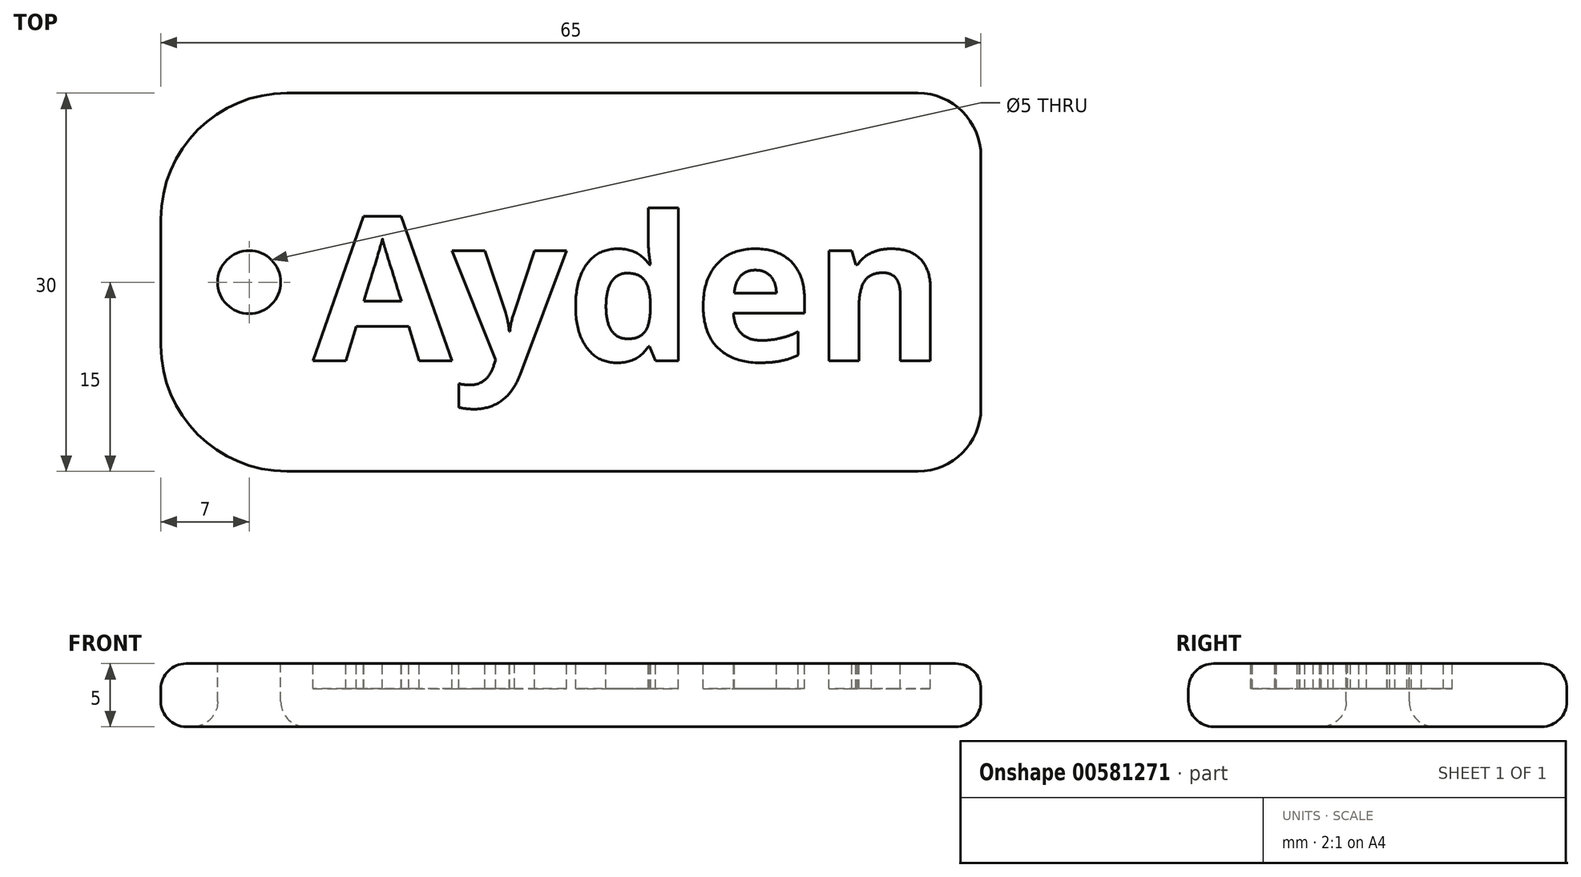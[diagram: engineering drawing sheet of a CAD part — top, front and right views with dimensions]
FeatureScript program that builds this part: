
annotation { "Feature Type Name" : "Feature", "Feature Type Description" : "" }
export const myFeature = defineFeature(function(context is Context, id is Id, definition is map)
    precondition{}
    {
        {
            var Q0;
            Q0=qCreatedBy(makeId("Top.planeOp"),FACE);
            var sketch = newSketch(context, id + "F0", { "sketchPlane" : qUnion([Q0])});
            skLineSegment(sketch, "E0.bottom", {"start": v(0, 0) * mm, "end": v(65, 0) * mm});
            skLineSegment(sketch, "E0.top", {"start": v(0, 30) * mm, "end": v(65, 30) * mm});
            skLineSegment(sketch, "E0.left", {"start": v(0, 0) * mm, "end": v(0, 30) * mm});
            skLineSegment(sketch, "E0.right", {"start": v(65, 0) * mm, "end": v(65, 30) * mm});
            skSolve(sketch);
        }
        {
            var Q0;
            Q0=makeQuery(id+"F0.imprint","IMPRINT",FACE,{"disambiguationData":[TD([[makeQuery(id+"F0.imprint","IMPRINT",EDGE,{"derivedFrom":sQuery(id+"F0.wireOp",EDGE,"E0.bottom")}),1.0]])]});
            extrude(context, id + "F1", {"entities" : qUnion([Q0]), "depth" : 5 * mm, "offsetDistance" : 25 * mm});
        }
        {
            var Q0;
            Q0=makeQuery(id+"F1.opExtrude","CAP_FACE",FACE,{"disambiguationData":[OSD([sQuery(id+"F0.wireOp",EDGE,"E0.bottom"),sQuery(id+"F0.wireOp",EDGE,"E0.top"),sQuery(id+"F0.wireOp",EDGE,"E0.left"),sQuery(id+"F0.wireOp",EDGE,"E0.right")])],"isStart":false});
            var sketch = newSketch(context, id + "F2", { "sketchPlane" : qUnion([Q0])});
            skCircle(sketch, "E1", {"center": v(7, 15) * mm, "radius": 2.5 * mm});
            skPoint(sketch, "E1.centerSnap0", {"position": v(0, 15) * mm});
            skSolve(sketch);
        }
        {
            var Q0;
            Q0=makeQuery(id+"F2.imprint","IMPRINT",FACE,{"disambiguationData":[TD([[makeQuery(id+"F2.imprint","IMPRINT",EDGE,{"derivedFrom":sQuery(id+"F2.wireOp",EDGE,"E1")}),1.0]])]});
            extrude(context, id + "F3", {"entities" : qUnion([Q0]), "operationType" : NewBodyOperationType.REMOVE, "endBound" : BoundingType.THROUGH_ALL, "oppositeDirection" : true, "depth" : 25 * mm, "offsetDistance" : 25 * mm});
        }
        {
            var Q0;
            Q0=makeQuery(id+"F1.opExtrude","SWEPT_EDGE",EDGE,{"disambiguationData":[OSD([sQuery(id+"F0.wireOp",EDGE,"E0.top"),sQuery(id+"F0.wireOp",EDGE,"E0.right")])]});
            var Q1;
            Q1=makeQuery(id+"F1.opExtrude","SWEPT_EDGE",EDGE,{"disambiguationData":[OSD([sQuery(id+"F0.wireOp",EDGE,"E0.bottom"),sQuery(id+"F0.wireOp",EDGE,"E0.right")])]});
            fillet(context, id + "F4", {"entities" : qUnion([Q0, Q1]), "radius" : 5 * mm, "tangentPropagation" : true, "allowEdgeOverflow" : false});
        }
        {
            var Q0;
            Q0=makeQuery(id+"F1.opExtrude","SWEPT_EDGE",EDGE,{"disambiguationData":[OSD([sQuery(id+"F0.wireOp",EDGE,"E0.top"),sQuery(id+"F0.wireOp",EDGE,"E0.left")])]});
            var Q1;
            Q1=makeQuery(id+"F1.opExtrude","SWEPT_EDGE",EDGE,{"disambiguationData":[OSD([sQuery(id+"F0.wireOp",EDGE,"E0.bottom"),sQuery(id+"F0.wireOp",EDGE,"E0.left")])]});
            fillet(context, id + "F5", {"entities" : qUnion([Q0, Q1]), "radius" : 10 * mm, "tangentPropagation" : true, "allowEdgeOverflow" : false});
        }
        {
            var Q0;
            Q0=makeQuery(id+"F1.opExtrude","CAP_FACE",FACE,{"disambiguationData":[OSD([sQuery(id+"F0.wireOp",EDGE,"E0.bottom"),sQuery(id+"F0.wireOp",EDGE,"E0.top"),sQuery(id+"F0.wireOp",EDGE,"E0.left"),sQuery(id+"F0.wireOp",EDGE,"E0.right")])],"isStart":false});
            var sketch = newSketch(context, id + "F6", { "sketchPlane" : qUnion([Q0])});
            skText(sketch, "E2", { "text": "Ayden", "fontName": "OpenSans-Bold.ttf"});
            const initialGuessF6  = {"E2": [0.01205, 0.00877, 1, 0, 0.0115]};
            skSetInitialGuess(sketch, initialGuessF6);
            skSolve(sketch);
        }
        {
            var Q0;
            Q0 = qSketchRegion(id + "F6", true);
            extrude(context, id + "F7", {"entities" : qUnion([Q0]), "operationType" : NewBodyOperationType.REMOVE, "oppositeDirection" : true, "depth" : 2 * mm, "offsetDistance" : 25 * mm});
        }
        {
            var Q0;
            Q0=makeQuery(id+"F1.opExtrude","CAP_EDGE",EDGE,{"disambiguationData":[OSD([sQuery(id+"F0.wireOp",EDGE,"E0.top")])],"isStart":false});
            var Q1;
            {var subQ0=sQuery(id+"F0.wireOp",EDGE,"E0.right");var subQ1=sQuery(id+"F0.wireOp",EDGE,"E0.top");Q1=makeQuery(id+"F4.opFillet","BLEND_EDGE",EDGE,{"blendedFrom":[makeQuery(id+"F1.opExtrude","SWEPT_EDGE",EDGE,{"disambiguationData":[OSD([subQ1,subQ0])]}),makeQuery(id+"F1.opExtrude","CAP_FACE",FACE,{"disambiguationData":[OSD([sQuery(id+"F0.wireOp",EDGE,"E0.bottom"),subQ1,sQuery(id+"F0.wireOp",EDGE,"E0.left"),subQ0])],"isStart":false})],"blendedInto":[makeQuery(id+"F1.opExtrude","CAP_FACE",FACE,{"disambiguationData":[OSD([sQuery(id+"F0.wireOp",EDGE,"E0.bottom"),subQ1,sQuery(id+"F0.wireOp",EDGE,"E0.left"),subQ0])],"isStart":false})]});}
            var Q2;
            Q2=makeQuery(id+"F1.opExtrude","CAP_FACE",FACE,{"disambiguationData":[OSD([sQuery(id+"F0.wireOp",EDGE,"E0.bottom"),sQuery(id+"F0.wireOp",EDGE,"E0.top"),sQuery(id+"F0.wireOp",EDGE,"E0.left"),sQuery(id+"F0.wireOp",EDGE,"E0.right")])],"isStart":true});
            var Q3;
            Q3=makeQuery(id+"F3.boolean.opBoolean","COPY",EDGE,{"derivedFrom":makeQuery(id+"F3.opExtrude","CAP_EDGE",EDGE,{"disambiguationData":[OSD([sQuery(id+"F2.wireOp",EDGE,"E1")])],"isStart":true})});
            fillet(context, id + "F8", {"entities" : qUnion([Q0, Q1, Q2, Q3]), "radius" : 2 * mm, "tangentPropagation" : true, "allowEdgeOverflow" : false});
        }
    });
